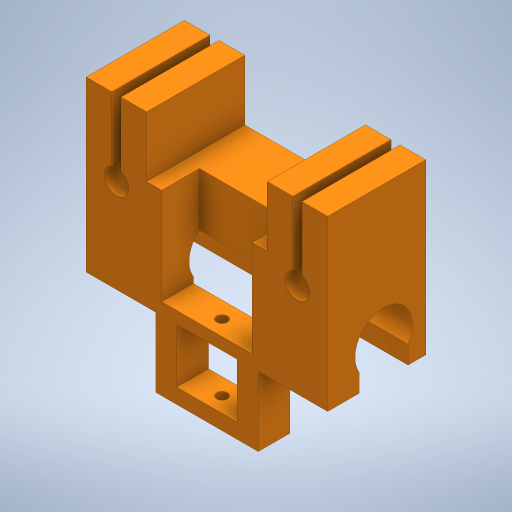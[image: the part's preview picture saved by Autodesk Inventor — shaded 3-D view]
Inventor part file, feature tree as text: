
AUTODESK INVENTOR PART (.ipt)
format: ipt  version: 2023 (Build 270158000, 158)  size: 483,840 bytes
history: native  units: mm
features: extrude x12, sketch x12, projected_geometry x6
ambient origin geometry x8: Origin, YZ Plane, XZ Plane, XY Plane, X Axis, Y Axis, Z Axis, Center Point
bodies: Solid1 (feature_tree)
feature tree (30):
  extrude  "Extrusion1"  Depth=10.0mm
  extrude  "Extrusion5"  Depth=1.5mm
  extrude  "Extrusion11"  Depth=10.0mm
  extrude  "Extrusion13"  Depth=80.0mm
  extrude  "Extrusion14"  TaperAngle=0.0deg  [1 undecoded]
  extrude  "Extrusion15"  Depth=20.0mm
  extrude  "Extrusion16"  Depth=20.0mm
  extrude  "Extrusion17"  Depth=10.0mm
  extrude  "Extrusion18"  Depth=20.0mm
  extrude  "Extrusion19"  Depth=35.0mm
  extrude  "Extrusion20"  Depth=80.0mm TaperAngle=0.0deg
  extrude  "Extrusion21"  Depth=20.0mm TaperAngle=0.0deg
  sketch  "Sketch1"  dims[d2=8.0mm d3=10.0mm]
  sketch  "Sketch5"  dims[d7=1.5mm d8=1.5mm]
  sketch  "Sketch13"  dims[d9=36.0mm d10=0.0mm d16=10.0mm]
  projected_geometry  "Projected Loop1"
  sketch  "Sketch16"  dims[d17=8.0mm d18=1.5mm d19=1.5mm d20=10.0mm d21=8.0mm d22=80.0mm]
  sketch  "Sketch17"  dims[d23=10.0mm d24=0.0mm]
  sketch  "Sketch18"  dims[d25=60.0mm d26=20.0mm]
  sketch  "Sketch19"  dims[d27=20.0mm d28=20.0mm]
  sketch  "Sketch20"  dims[d29=20.0mm d30=10.0mm]
  sketch  "Sketch21"  dims[d31=10.0mm d32=20.0mm]
  projected_geometry  "Projected Loop2"
  sketch  "Sketch22"  dims[d40=30.0mm d41=35.0mm]
  projected_geometry  "Projected Loop3"
  projected_geometry  "Projected Loop4"
  projected_geometry  "Projected Loop5"
  sketch  "Sketch23"  dims[d45=20.0mm d46=80.0mm d47=0.0mm]
  sketch  "Sketch24"  dims[d79=25.0mm d82=25.0mm d83=1.0mm d84=0.0mm d85=19.0mm d86=5.0mm d87=15.0mm d103=6.0mm d104=0.0mm d105=20.0mm d106=0.0mm d107=30.0mm d108=25.0mm d109=15.0mm d110=0.0mm d111=37.0mm d112=0.0mm d113=7.0mm d114=7.0mm d115=5.0mm d116=18.0mm d117=20.0mm d118=23.0mm d119=15.5mm d120=0.0mm d121=3.5mm d122=7.5mm d123=40.0mm d124=80.0mm d125=0.0mm d126=2.5mm d127=0.0mm d128=15.0mm d129=0.0mm d130=20.0mm d131=20.0mm d132=20.0mm d133=0.0mm d134=2.5mm d135=0.0mm]
  projected_geometry  "Projected Loop6"
note: 1 required parameter value undecoded (feature->parameter linkage not recoverable at this tier; creation-order binding heuristic only, values carry confidence <= 0.55)
